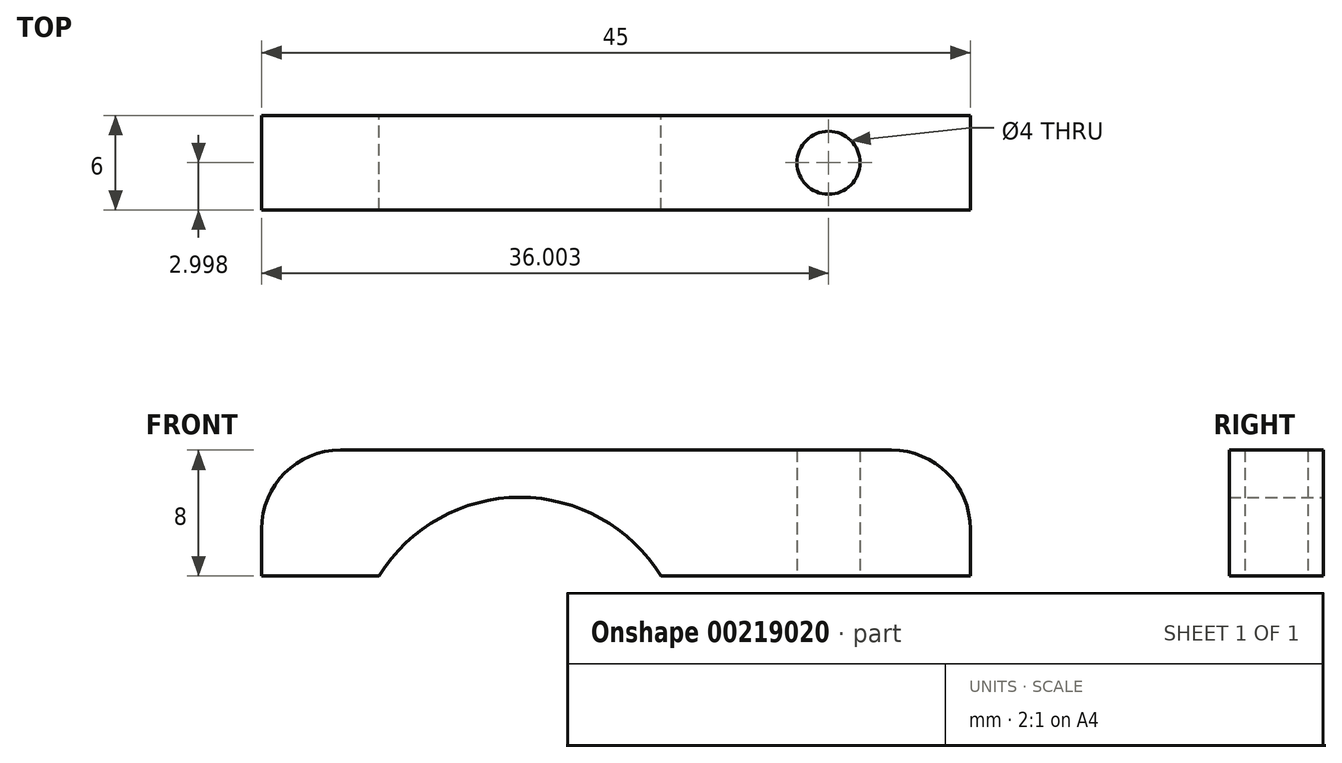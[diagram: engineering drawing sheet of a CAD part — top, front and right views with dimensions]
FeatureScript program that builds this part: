
annotation { "Feature Type Name" : "Feature", "Feature Type Description" : "" }
export const myFeature = defineFeature(function(context is Context, id is Id, definition is map)
    precondition{}
    {
        {
            var Q0;
            Q0=qCreatedBy(makeId("Top.planeOp"),FACE);
            var sketch = newSketch(context, id + "F0", { "sketchPlane" : qUnion([Q0])});
            skLineSegment(sketch, "E0.bottom", {"start": v(-22.35, -0.14) * mm, "end": v(22.65, -0.14) * mm});
            skLineSegment(sketch, "E0.top", {"start": v(-22.35, -6.14) * mm, "end": v(22.65, -6.14) * mm});
            skLineSegment(sketch, "E0.left", {"start": v(-22.35, -0.14) * mm, "end": v(-22.35, -6.14) * mm});
            skLineSegment(sketch, "E0.right", {"start": v(22.65, -0.14) * mm, "end": v(22.65, -6.14) * mm});
            skLineSegment(sketch, "E1", {"start": v(-22.35, -3.14) * mm, "end": v(13.65, -3.14) * mm, "construction": true});
            skCircle(sketch, "E2", {"center": v(13.65, -3.14) * mm, "radius": 2 * mm});
            skSolve(sketch);
        }
        {
            var Q0;
            Q0=makeQuery(id+"F0.imprint","IMPRINT",FACE,{"disambiguationData":[TD([[makeQuery(id+"F0.imprint","IMPRINT",EDGE,{"derivedFrom":sQuery(id+"F0.wireOp",EDGE,"E0.bottom")}),-1.0]])]});
            extrude(context, id + "F1", {"entities" : qUnion([Q0]), "depth" : 8 * mm});
        }
        {
            var Q0;
            Q0=qCreatedBy(makeId("Front.planeOp"),FACE);
            var sketch = newSketch(context, id + "F2", { "sketchPlane" : qUnion([Q0])});
            skLineSegment(sketch, "E3", {"start": v(-22.3, 0) * mm, "end": v(-16.3, 0) * mm, "construction": true});
            skCircle(sketch, "E4", {"center": v(-5.94, -5.5) * mm, "radius": 10.5 * mm});
            skSolve(sketch);
        }
        {
            var Q0;
            Q0 = qSketchRegion(id + "F2", true);
            extrude(context, id + "F3", {"entities" : qUnion([Q0]), "operationType" : NewBodyOperationType.REMOVE, "depth" : 8 * mm});
        }
        {
            var Q0;
            Q0=makeQuery(id+"F1.opExtrude","CAP_EDGE",EDGE,{"disambiguationData":[OSD([sQuery(id+"F0.wireOp",EDGE,"E0.left")])],"isStart":false});
            fillet(context, id + "F4", {"entities" : qUnion([Q0]), "radius" : 5 * mm, "tangentPropagation" : true, "allowEdgeOverflow" : false});
        }
        {
            var Q0;
            Q0=makeQuery(id+"F1.opExtrude","CAP_EDGE",EDGE,{"disambiguationData":[OSD([sQuery(id+"F0.wireOp",EDGE,"E0.right")])],"isStart":false});
            fillet(context, id + "F5", {"entities" : qUnion([Q0]), "radius" : 5 * mm, "tangentPropagation" : true, "allowEdgeOverflow" : false});
        }
    });
